# Revit family: Water_Heaters_HAJDU_HAJDU-HD-200-300_
name_source: partatom
category: Mechanical Equipment
units: mm (PartAtom-declared; Revit-internal decimal feet)

## family parameters
Always vertical = Yes
Classification = None
Cut with Voids When Loaded = No
Maintain Annotation Orientation = No
OmniClass Number = 23.31.29.13
OmniClass Title = Hot Water Tank Heaters
Part Type = Normal
Room Calculation Point = No
Round Connector Dimension = Use Diameter
Shared = No
Work Plane-Based = Yes

## types (2) — shared parameters
Case Material = Hajdu - Felület - Fehér
Církulációs csonk = 25.4 mm  [stored 0.0833333 ft]
Default Elevation = 1219.2 mm  [stored 4 ft]
Description = A HD típusú, külső hőcserélővel fűthető tárolók, intézményi, társasházi hőközpontokba, távhőellátási alközpontokba ajánlottak. A melegvíz előállítás átfolyós üzemmódban történik, a tárolónak csúcsigény csillapító, kiegyenlítő szerepe van. A termékcsalád mindegyike nagy nyomásállóságú és nagy átmérőjű csatlakozással rendelkezik.
Energiahatékonysági osztály = C
Homéro csonk = 12.7 mm  [stored 0.0416667 ft]
Korrózióvédelem = tűzzománc + 2db külső áramforrású anód
Magasság = 1530 mm  [stored 5.01969 ft]
Manufacturer = HAJDU
Product Page URL = https://hajdurt.hu
Tartály = tűzzománcozott acéllemez
URL = https://hajdurt.hu
Vízcsatlakozás = 31.75 mm
Érzékelo tokcso = 12.7 mm  [stored 0.0416667 ft]
Üzemi nyomás = 1.0 MPa

## per-type parameters (varying)
| type | Csatlakozó magassága "A" | Csatlakozó magassága "B" | Csatlakozó magassága "C" | Névleges urtartalom | Rádiusz | Tárolási veszteség | Tömeg | Átméro |
| HD 200 | 975 mm  [stored 3.19882 ft] | 1273 mm  [stored 4.17651 ft] | 1411.23 mm | 200 l | 272.5 mm  [stored 0.894029 ft] | 83 W | 87.00 kg | 545 mm  [stored 1.78806 ft] |
| HD 300 | 1025 mm  [stored 3.36286 ft] | 1252 mm  [stored 4.10761 ft] | 1387 mm  [stored 4.55052 ft] | 300 l | 330 mm  [stored 1.08268 ft] | 94 W | 120.00 kg | 660 mm |

note: column(s) folded — value = type name in every type: Model

note: [stored X ft] marks values corroborated as IEEE doubles in the binary element streams (Revit-internal decimal feet)

## geometry (parser evidence)
native form markers: Sweep x3
no freeform markers — native parametric forms only
